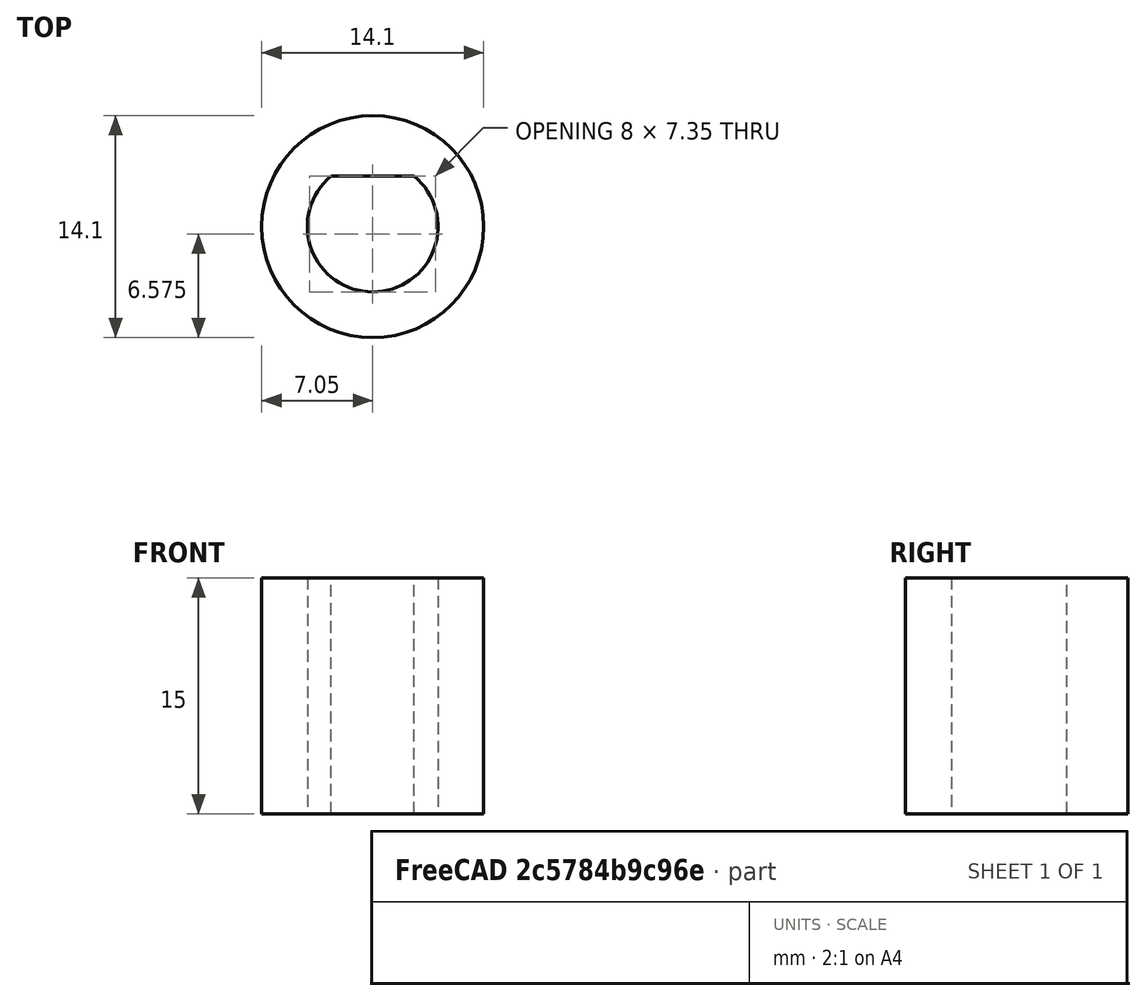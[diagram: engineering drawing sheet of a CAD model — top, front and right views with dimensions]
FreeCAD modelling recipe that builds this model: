
FCSTD DOCUMENT  (FreeCAD 0.21R33771 (Git))
Label: RiduzioneAlbero8-14
License: All rights reserved
LicenseURL: https://en.wikipedia.org/wiki/All_rights_reserved
objects: Sketcher::SketchObject×1, PartDesign::Pad×1, PartDesign::Body×1
note: 4 computed .brp shape members not serialized (recipe doc carries the construction recipe); baked Part::Feature solids carry a one-line shape summary decoded from their .brp

FEATURE [Sketcher::SketchObject] Sketch
  FullyConstrained = true
  MapMode = 5
  Support = -> [XY_Plane]
  sketch-geometry (3):
    g0: ArcOfCircle CenterX=0 CenterY=0 CenterZ=0 NormalX=0 NormalY=0 NormalZ=1 AngleXU=0 Radius=4.15 StartAngle=2.26105 EndAngle=7.16373
    g1: LineSegment StartX=-2.64244 StartY=3.2 StartZ=0 EndX=2.64244 EndY=3.2 EndZ=0
    g2: Circle CenterX=0 CenterY=0 CenterZ=0 NormalX=0 NormalY=0 NormalZ=1 AngleXU=0 Radius=7.05
  constraints (8):
    c: Coincident(g0,g-1)
    c: Horizontal(g1)
    c: Coincident(g1,g0)
    c: Coincident(g1,g0)
    c: Radius(g0) = 4.15
    c: DistanceY(g0,g0) = 3.2
    c: Coincident(g2,g0)
    c: Radius(g2) = 7.05
FEATURE [PartDesign::Pad] Pad
  Direction = (0,0,1)
  Length = 15
  Length2 = 10
  Profile = -> Sketch
  ReferenceAxis = -> Sketch [N_Axis]
  Type = 0
FEATURE [PartDesign::Body] Body
  Group = -> [Sketch,Pad]
  Origin = -> Origin
  Tip = -> Pad
